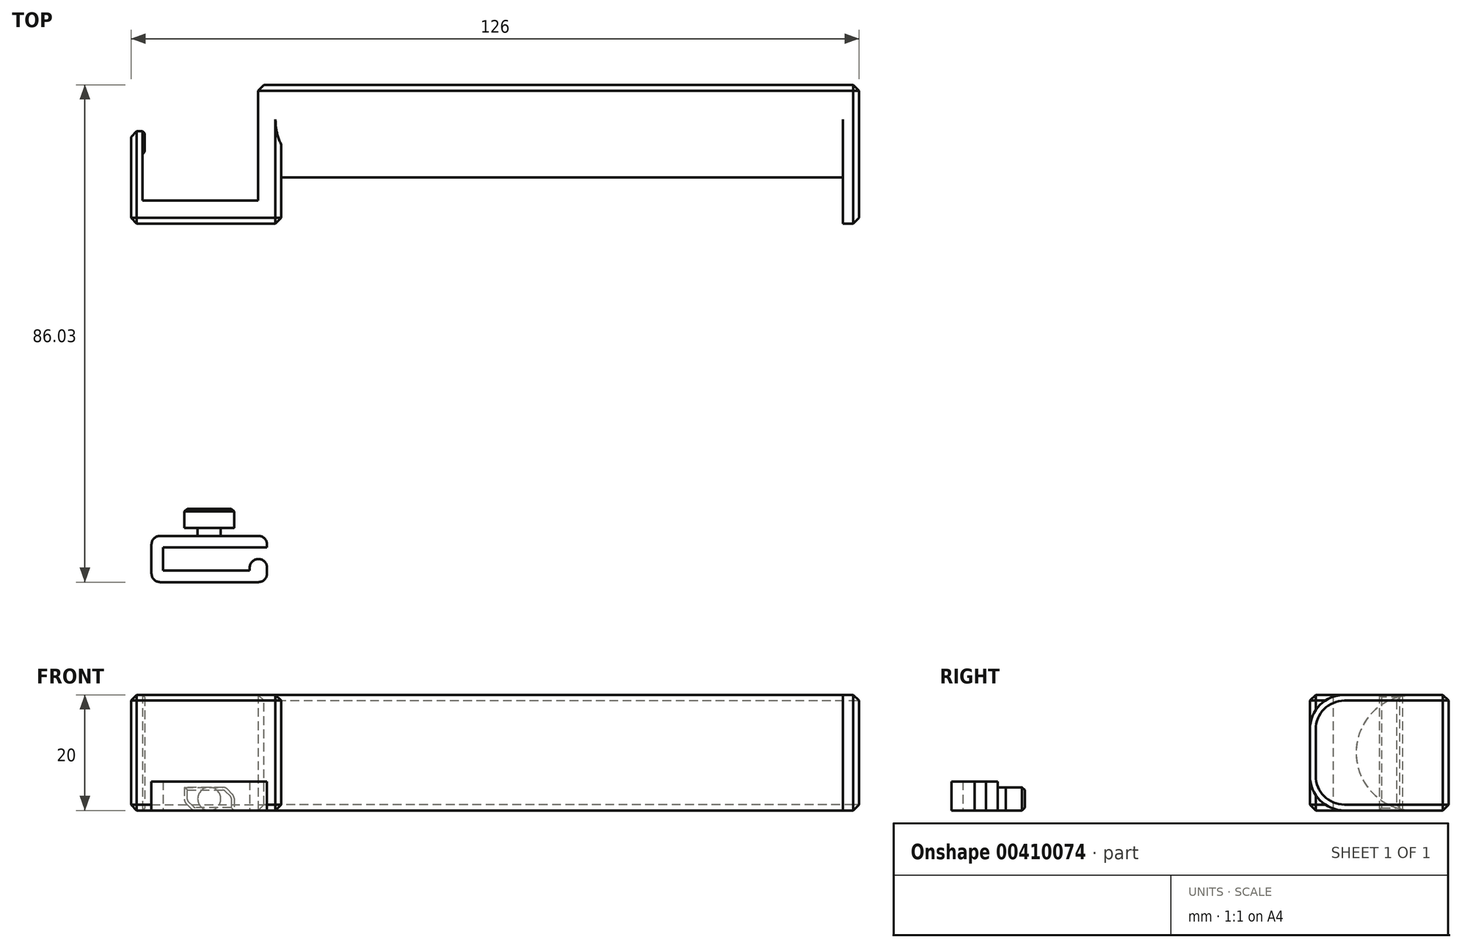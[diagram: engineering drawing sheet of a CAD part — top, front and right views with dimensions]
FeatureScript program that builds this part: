
annotation { "Feature Type Name" : "Feature", "Feature Type Description" : "" }
export const myFeature = defineFeature(function(context is Context, id is Id, definition is map)
    precondition{}
    {
        {
            var Q0;
            Q0=qCreatedBy(makeId("Top.planeOp"),FACE);
            var sketch = newSketch(context, id + "F0", { "sketchPlane" : qUnion([Q0])});
            skLineSegment(sketch, "E0.top", {"start": v(-65.92, 21.88) * mm, "end": v(-45.92, 21.88) * mm});
            skLineSegment(sketch, "E0.left", {"start": v(-65.92, 33.88) * mm, "end": v(-65.92, 21.88) * mm});
            skLineSegment(sketch, "E0.right", {"start": v(-45.92, 41.88) * mm, "end": v(-45.92, 21.88) * mm});
            skLineSegment(sketch, "E1.top", {"start": v(-67.92, 17.88) * mm, "end": v(-41.92, 17.88) * mm});
            skLineSegment(sketch, "E1.left", {"start": v(-67.92, 33.88) * mm, "end": v(-67.92, 17.88) * mm});
            skLineSegment(sketch, "E1.right", {"start": v(-41.92, 41.88) * mm, "end": v(-41.92, 17.88) * mm});
            skLineSegment(sketch, "E2.bottom", {"start": v(-41.92, 41.88) * mm, "end": v(58.08, 41.88) * mm});
            skLineSegment(sketch, "E2.top", {"start": v(-41.92, 25.88) * mm, "end": v(58.08, 25.88) * mm});
            skLineSegment(sketch, "E2.left", {"start": v(-41.92, 41.88) * mm, "end": v(-41.92, 25.88) * mm});
            skLineSegment(sketch, "E2.right", {"start": v(58.08, 41.88) * mm, "end": v(58.08, 25.88) * mm});
            skLineSegment(sketch, "E3.trimOffspring", {"start": v(-45.92, 41.88) * mm, "end": v(-41.92, 41.88) * mm});
            skLineSegment(sketch, "E4", {"start": v(-65.92, 33.88) * mm, "end": v(-65.52, 33.88) * mm});
            skLineSegment(sketch, "E5", {"start": v(-65.52, 33.88) * mm, "end": v(-65.52, 29.88) * mm});
            skLineSegment(sketch, "E6", {"start": v(-65.52, 29.88) * mm, "end": v(-65.92, 29.88) * mm});
            skLineSegment(sketch, "E7", {"start": v(58.08, 25.88) * mm, "end": v(58.08, 17.88) * mm});
            skLineSegment(sketch, "E8", {"start": v(58.08, 17.88) * mm, "end": v(55.28, 17.88) * mm});
            skLineSegment(sketch, "E9", {"start": v(55.28, 17.88) * mm, "end": v(55.28, 25.88) * mm});
            skLineSegment(sketch, "E10", {"start": v(-65.92, 33.88) * mm, "end": v(-67.92, 33.88) * mm});
            skPoint(sketch, "E1.bottom.end.orphan", {"position": v(-65.92, 41.88) * mm});
            skPoint(sketch, "E1.bottom.start.orphan", {"position": v(-67.92, 41.88) * mm});
            skSolve(sketch);
        }
        {
            var Q0;
            Q0=qSketchRegion(id+"F0",true);
            extrude(context, id + "F1", {"entities" : qUnion([Q0]), "depth" : 20 * mm});
        }
        {
            var Q0;
            Q0=makeQuery(id+"F1.opExtrude","CAP_EDGE",EDGE,{"disambiguationData":[OSD([sQuery(id+"F0.wireOp",EDGE,"E2.top")])],"isStart":false});
            var Q1;
            Q1=makeQuery(id+"F1.opExtrude","CAP_EDGE",EDGE,{"disambiguationData":[OSD([sQuery(id+"F0.wireOp",EDGE,"E2.top")])],"isStart":true});
            fillet(context, id + "F2", {"entities" : qUnion([Q0, Q1]), "radius" : 10 * mm, "tangentPropagation" : true, "allowEdgeOverflow" : false});
        }
        {
            var Q0;
            Q0=makeQuery(id+"F1.opExtrude","CAP_EDGE",EDGE,{"disambiguationData":[OSD([sQuery(id+"F0.wireOp",EDGE,"E8")])],"isStart":false});
            var Q1;
            Q1=makeQuery(id+"F1.opExtrude","CAP_EDGE",EDGE,{"disambiguationData":[OSD([sQuery(id+"F0.wireOp",EDGE,"E8")])],"isStart":true});
            fillet(context, id + "F3", {"entities" : qUnion([Q0, Q1]), "radius" : 6 * mm, "tangentPropagation" : true, "allowEdgeOverflow" : false});
        }
        {
            var Q0;
            Q0=makeQuery(id+"F1.opExtrude","SWEPT_FACE",FACE,{"disambiguationData":[OSD([sQuery(id+"F0.wireOp",EDGE,"E2.bottom"),sQuery(id+"F0.wireOp",EDGE,"E3.trimOffspring")])]});
            var Q1;
            Q1=makeQuery(id+"F1.opExtrude","SWEPT_FACE",FACE,{"disambiguationData":[OSD([sQuery(id+"F0.wireOp",EDGE,"E1.top")])]});
            var Q2;
            Q2=makeQuery(id+"F1.opExtrude","CAP_EDGE",EDGE,{"disambiguationData":[OSD([sQuery(id+"F0.wireOp",EDGE,"E1.right")])],"isStart":false});
            var Q3;
            Q3=makeQuery(id+"F1.opExtrude","CAP_EDGE",EDGE,{"disambiguationData":[OSD([sQuery(id+"F0.wireOp",EDGE,"E1.right")])],"isStart":true});
            var Q4;
            Q4=makeQuery(id+"F1.opExtrude","SWEPT_FACE",FACE,{"disambiguationData":[OSD([sQuery(id+"F0.wireOp",EDGE,"E2.right"),sQuery(id+"F0.wireOp",EDGE,"E7")])]});
            var Q5;
            Q5=makeQuery(id+"F1.opExtrude","SWEPT_FACE",FACE,{"disambiguationData":[OSD([sQuery(id+"F0.wireOp",EDGE,"E1.left")])]});
            chamfer(context, id + "F4", {"entities" : qUnion([Q0, Q1, Q2, Q3, Q4, Q5]), "width" : 1 * mm, "tangentPropagation" : true});
        }
        {
            var Q0;
            Q0=makeQuery(id+"F1.opExtrude","SWEPT_FACE",FACE,{"disambiguationData":[OSD([sQuery(id+"F0.wireOp",EDGE,"E5")])]});
            chamfer(context, id + "F5", {"entities" : qUnion([Q0]), "width" : 0.4 * mm, "tangentPropagation" : true});
        }
        {
            var Q0;
            Q0=qCreatedBy(makeId("Top.planeOp"),FACE);
            var sketch = newSketch(context, id + "F6", { "sketchPlane" : qUnion([Q0])});
            skLineSegment(sketch, "E11.bottom", {"start": v(-58.68, -34.75) * mm, "end": v(-50.08, -34.75) * mm});
            skLineSegment(sketch, "E11.top", {"start": v(-58.68, -31.45) * mm, "end": v(-50.08, -31.45) * mm});
            skLineSegment(sketch, "E11.left", {"start": v(-58.68, -34.75) * mm, "end": v(-58.68, -31.45) * mm});
            skLineSegment(sketch, "E11.right", {"start": v(-50.08, -34.75) * mm, "end": v(-50.08, -31.45) * mm});
            skLineSegment(sketch, "E12", {"start": v(-56.38, -34.75) * mm, "end": v(-56.38, -36.15) * mm});
            skLineSegment(sketch, "E13", {"start": v(-56.38, -36.15) * mm, "end": v(-52.38, -36.15) * mm});
            skLineSegment(sketch, "E14", {"start": v(-52.38, -36.15) * mm, "end": v(-52.38, -34.75) * mm});
            skLineSegment(sketch, "E15.bottom", {"start": v(-64.38, -36.15) * mm, "end": v(-44.38, -36.15) * mm});
            skLineSegment(sketch, "E15.top", {"start": v(-64.38, -44.15) * mm, "end": v(-44.38, -44.15) * mm});
            skLineSegment(sketch, "E15.left", {"start": v(-64.38, -36.15) * mm, "end": v(-64.38, -44.15) * mm});
            skLineSegment(sketch, "E15.right", {"start": v(-44.38, -36.15) * mm, "end": v(-44.38, -38.15) * mm});
            skLineSegment(sketch, "E16", {"start": v(-44.38, -42.15) * mm, "end": v(-62.38, -42.15) * mm});
            skLineSegment(sketch, "E17", {"start": v(-62.38, -42.15) * mm, "end": v(-62.38, -38.15) * mm});
            skLineSegment(sketch, "E18", {"start": v(-62.38, -38.15) * mm, "end": v(-44.38, -38.15) * mm});
            skLineSegment(sketch, "E19", {"start": v(-47.38, -42.15) * mm, "end": v(-47.38, -40.15) * mm});
            skLineSegment(sketch, "E20", {"start": v(-47.38, -40.15) * mm, "end": v(-44.38, -40.15) * mm});
            skPoint(sketch, "E20.endSnap0", {"position": v(-44.38, -40.15) * mm});
            skLineSegment(sketch, "E21.trimOffspring", {"start": v(-44.38, -40.15) * mm, "end": v(-44.38, -44.15) * mm});
            skSolve(sketch);
        }
        {
            var Q0;
            Q0=qSketchRegion(id+"F6",true);
            extrude(context, id + "F7", {"entities" : qUnion([Q0]), "depth" : 4 * mm});
        }
        {
            var Q0;
            Q0=makeQuery(id+"F7.opExtrude","CAP_EDGE",EDGE,{"disambiguationData":[OSD([sQuery(id+"F6.wireOp",EDGE,"E12")])],"isStart":true});
            var Q1;
            Q1=makeQuery(id+"F7.opExtrude","CAP_EDGE",EDGE,{"disambiguationData":[OSD([sQuery(id+"F6.wireOp",EDGE,"E14")])],"isStart":true});
            var Q2;
            Q2=makeQuery(id+"F7.opExtrude","CAP_EDGE",EDGE,{"disambiguationData":[OSD([sQuery(id+"F6.wireOp",EDGE,"E14")])],"isStart":false});
            var Q3;
            Q3=makeQuery(id+"F7.opExtrude","CAP_EDGE",EDGE,{"disambiguationData":[OSD([sQuery(id+"F6.wireOp",EDGE,"E12")])],"isStart":false});
            fillet(context, id + "F8", {"entities" : qUnion([Q0, Q1, Q2, Q3]), "radius" : 2 * mm, "tangentPropagation" : true, "allowEdgeOverflow" : false});
        }
        {
            var Q0;
            Q0=makeQuery(id+"F7.opExtrude","CAP_EDGE",EDGE,{"disambiguationData":[OSD([sQuery(id+"F6.wireOp",EDGE,"E11.right")])],"isStart":false});
            var Q1;
            Q1=makeQuery(id+"F7.opExtrude","CAP_EDGE",EDGE,{"disambiguationData":[OSD([sQuery(id+"F6.wireOp",EDGE,"E11.left")])],"isStart":true});
            chamfer(context, id + "F9", {"entities" : qUnion([Q0, Q1]), "width" : 1.5 * mm, "tangentPropagation" : true});
        }
        {
            var Q0;
            {var subQ0=sQuery(id+"F6.wireOp",EDGE,"E11.right");Q0=makeQuery(id+"F9.opChamfer","BLEND_EDGE",EDGE,{"blendedFrom":[makeQuery(id+"F7.opExtrude","CAP_EDGE",EDGE,{"disambiguationData":[OSD([subQ0])],"isStart":false}),makeQuery(id+"F7.opExtrude","SWEPT_FACE",FACE,{"disambiguationData":[OSD([subQ0])]})],"blendedInto":[makeQuery(id+"F7.opExtrude","SWEPT_FACE",FACE,{"disambiguationData":[OSD([subQ0])]})]});}
            var Q1;
            {var subQ0=sQuery(id+"F6.wireOp",EDGE,"E11.right");Q1=makeQuery(id+"F9.opChamfer","BLEND_EDGE",EDGE,{"blendedFrom":[makeQuery(id+"F7.opExtrude","CAP_EDGE",EDGE,{"disambiguationData":[OSD([subQ0])],"isStart":false}),makeQuery(id+"F8.opFillet","SPLIT",FACE,{"disambiguationData":[OD(0.0)],"derivedFrom":makeQuery(id+"F7.opExtrude","CAP_FACE",FACE,{"disambiguationData":[OSD([sQuery(id+"F6.wireOp",EDGE,"E11.bottom"),sQuery(id+"F6.wireOp",EDGE,"E11.top"),sQuery(id+"F6.wireOp",EDGE,"E11.left"),subQ0,sQuery(id+"F6.wireOp",EDGE,"E12"),sQuery(id+"F6.wireOp",EDGE,"E14"),sQuery(id+"F6.wireOp",EDGE,"E15.bottom"),sQuery(id+"F6.wireOp",EDGE,"E15.top"),sQuery(id+"F6.wireOp",EDGE,"E15.left"),sQuery(id+"F6.wireOp",EDGE,"E15.right"),sQuery(id+"F6.wireOp",EDGE,"E16"),sQuery(id+"F6.wireOp",EDGE,"E17"),sQuery(id+"F6.wireOp",EDGE,"E18"),sQuery(id+"F6.wireOp",EDGE,"E19"),sQuery(id+"F6.wireOp",EDGE,"E20"),sQuery(id+"F6.wireOp",EDGE,"E21.trimOffspring")])],"isStart":false})})],"blendedInto":[makeQuery(id+"F8.opFillet","SPLIT",FACE,{"disambiguationData":[OD(0.0)],"derivedFrom":makeQuery(id+"F7.opExtrude","CAP_FACE",FACE,{"disambiguationData":[OSD([sQuery(id+"F6.wireOp",EDGE,"E11.bottom"),sQuery(id+"F6.wireOp",EDGE,"E11.top"),sQuery(id+"F6.wireOp",EDGE,"E11.left"),subQ0,sQuery(id+"F6.wireOp",EDGE,"E12"),sQuery(id+"F6.wireOp",EDGE,"E14"),sQuery(id+"F6.wireOp",EDGE,"E15.bottom"),sQuery(id+"F6.wireOp",EDGE,"E15.top"),sQuery(id+"F6.wireOp",EDGE,"E15.left"),sQuery(id+"F6.wireOp",EDGE,"E15.right"),sQuery(id+"F6.wireOp",EDGE,"E16"),sQuery(id+"F6.wireOp",EDGE,"E17"),sQuery(id+"F6.wireOp",EDGE,"E18"),sQuery(id+"F6.wireOp",EDGE,"E19"),sQuery(id+"F6.wireOp",EDGE,"E20"),sQuery(id+"F6.wireOp",EDGE,"E21.trimOffspring")])],"isStart":false})})]});}
            var Q2;
            {var subQ0=sQuery(id+"F6.wireOp",EDGE,"E11.left");Q2=makeQuery(id+"F9.opChamfer","BLEND_EDGE",EDGE,{"blendedFrom":[makeQuery(id+"F7.opExtrude","CAP_EDGE",EDGE,{"disambiguationData":[OSD([subQ0])],"isStart":true}),makeQuery(id+"F7.opExtrude","SWEPT_FACE",FACE,{"disambiguationData":[OSD([subQ0])]})],"blendedInto":[makeQuery(id+"F7.opExtrude","SWEPT_FACE",FACE,{"disambiguationData":[OSD([subQ0])]})]});}
            var Q3;
            {var subQ0=sQuery(id+"F6.wireOp",EDGE,"E11.left");Q3=makeQuery(id+"F9.opChamfer","BLEND_EDGE",EDGE,{"blendedFrom":[makeQuery(id+"F7.opExtrude","CAP_EDGE",EDGE,{"disambiguationData":[OSD([subQ0])],"isStart":true}),makeQuery(id+"F8.opFillet","SPLIT",FACE,{"disambiguationData":[OD(0.0)],"derivedFrom":makeQuery(id+"F7.opExtrude","CAP_FACE",FACE,{"disambiguationData":[OSD([sQuery(id+"F6.wireOp",EDGE,"E11.bottom"),sQuery(id+"F6.wireOp",EDGE,"E11.top"),subQ0,sQuery(id+"F6.wireOp",EDGE,"E11.right"),sQuery(id+"F6.wireOp",EDGE,"E12"),sQuery(id+"F6.wireOp",EDGE,"E14"),sQuery(id+"F6.wireOp",EDGE,"E15.bottom"),sQuery(id+"F6.wireOp",EDGE,"E15.top"),sQuery(id+"F6.wireOp",EDGE,"E15.left"),sQuery(id+"F6.wireOp",EDGE,"E15.right"),sQuery(id+"F6.wireOp",EDGE,"E16"),sQuery(id+"F6.wireOp",EDGE,"E17"),sQuery(id+"F6.wireOp",EDGE,"E18"),sQuery(id+"F6.wireOp",EDGE,"E19"),sQuery(id+"F6.wireOp",EDGE,"E20"),sQuery(id+"F6.wireOp",EDGE,"E21.trimOffspring")])],"isStart":true})})],"blendedInto":[makeQuery(id+"F8.opFillet","SPLIT",FACE,{"disambiguationData":[OD(0.0)],"derivedFrom":makeQuery(id+"F7.opExtrude","CAP_FACE",FACE,{"disambiguationData":[OSD([sQuery(id+"F6.wireOp",EDGE,"E11.bottom"),sQuery(id+"F6.wireOp",EDGE,"E11.top"),subQ0,sQuery(id+"F6.wireOp",EDGE,"E11.right"),sQuery(id+"F6.wireOp",EDGE,"E12"),sQuery(id+"F6.wireOp",EDGE,"E14"),sQuery(id+"F6.wireOp",EDGE,"E15.bottom"),sQuery(id+"F6.wireOp",EDGE,"E15.top"),sQuery(id+"F6.wireOp",EDGE,"E15.left"),sQuery(id+"F6.wireOp",EDGE,"E15.right"),sQuery(id+"F6.wireOp",EDGE,"E16"),sQuery(id+"F6.wireOp",EDGE,"E17"),sQuery(id+"F6.wireOp",EDGE,"E18"),sQuery(id+"F6.wireOp",EDGE,"E19"),sQuery(id+"F6.wireOp",EDGE,"E20"),sQuery(id+"F6.wireOp",EDGE,"E21.trimOffspring")])],"isStart":true})})]});}
            fillet(context, id + "F10", {"entities" : qUnion([Q0, Q1, Q2, Q3]), "radius" : 1 * mm, "tangentPropagation" : true, "allowEdgeOverflow" : false});
        }
        {
            var Q0;
            Q0=makeQuery(id+"F7.opExtrude","SWEPT_FACE",FACE,{"disambiguationData":[OSD([sQuery(id+"F6.wireOp",EDGE,"E11.top")])]});
            chamfer(context, id + "F11", {"entities" : qUnion([Q0]), "width" : 0.5 * mm, "tangentPropagation" : true});
        }
        {
            var Q0;
            Q0=makeQuery(id+"F7.opExtrude","SWEPT_EDGE",EDGE,{"disambiguationData":[OSD([sQuery(id+"F6.wireOp",EDGE,"E20"),sQuery(id+"F6.wireOp",EDGE,"E21.trimOffspring")])]});
            var Q1;
            Q1=makeQuery(id+"F7.opExtrude","SWEPT_EDGE",EDGE,{"disambiguationData":[OSD([sQuery(id+"F6.wireOp",EDGE,"E19"),sQuery(id+"F6.wireOp",EDGE,"E20")])]});
            var Q2;
            Q2=makeQuery(id+"F7.opExtrude","SWEPT_EDGE",EDGE,{"disambiguationData":[OSD([sQuery(id+"F6.wireOp",EDGE,"E15.top"),sQuery(id+"F6.wireOp",EDGE,"E15.left")])]});
            var Q3;
            Q3=makeQuery(id+"F7.opExtrude","SWEPT_EDGE",EDGE,{"disambiguationData":[OSD([sQuery(id+"F6.wireOp",EDGE,"E15.bottom"),sQuery(id+"F6.wireOp",EDGE,"E15.left")])]});
            var Q4;
            Q4=makeQuery(id+"F7.opExtrude","SWEPT_EDGE",EDGE,{"disambiguationData":[OSD([sQuery(id+"F6.wireOp",EDGE,"E15.top"),sQuery(id+"F6.wireOp",EDGE,"E21.trimOffspring")])]});
            var Q5;
            Q5=makeQuery(id+"F7.opExtrude","SWEPT_EDGE",EDGE,{"disambiguationData":[OSD([sQuery(id+"F6.wireOp",EDGE,"E15.bottom"),sQuery(id+"F6.wireOp",EDGE,"E15.right")])]});
            fillet(context, id + "F12", {"entities" : qUnion([Q0, Q1, Q2, Q3, Q4, Q5]), "radius" : 1.5 * mm, "tangentPropagation" : true, "allowEdgeOverflow" : false});
        }
        {
            var Q0;
            Q0=makeQuery(id+"F8.opFillet","SPLIT",FACE,{"disambiguationData":[OD(1.0)],"derivedFrom":makeQuery(id+"F7.opExtrude","CAP_FACE",FACE,{"disambiguationData":[OSD([sQuery(id+"F6.wireOp",EDGE,"E11.bottom"),sQuery(id+"F6.wireOp",EDGE,"E11.top"),sQuery(id+"F6.wireOp",EDGE,"E11.left"),sQuery(id+"F6.wireOp",EDGE,"E11.right"),sQuery(id+"F6.wireOp",EDGE,"E12"),sQuery(id+"F6.wireOp",EDGE,"E14"),sQuery(id+"F6.wireOp",EDGE,"E15.bottom"),sQuery(id+"F6.wireOp",EDGE,"E15.top"),sQuery(id+"F6.wireOp",EDGE,"E15.left"),sQuery(id+"F6.wireOp",EDGE,"E15.right"),sQuery(id+"F6.wireOp",EDGE,"E16"),sQuery(id+"F6.wireOp",EDGE,"E17"),sQuery(id+"F6.wireOp",EDGE,"E18"),sQuery(id+"F6.wireOp",EDGE,"E19"),sQuery(id+"F6.wireOp",EDGE,"E20"),sQuery(id+"F6.wireOp",EDGE,"E21.trimOffspring")])],"isStart":false})});
            extrude(context, id + "F13", {"entities" : qUnion([Q0]), "operationType" : NewBodyOperationType.ADD, "depth" : 1 * mm});
        }
    });
